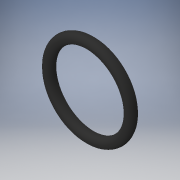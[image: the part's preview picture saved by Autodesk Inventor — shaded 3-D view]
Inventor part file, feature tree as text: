
AUTODESK INVENTOR PART (.ipt)
format: ipt  version: 2018 (Build 220112000, 112)  size: 136,704 bytes
history: native  units: in
note: dims shown in document units (in); Inventor stores cm internally (conversion verified against a paired STEP export)
features: revolve x1
ambient origin geometry x8: Origin, YZ Plane, XZ Plane, XY Plane, X Axis, Y Axis, Z Axis, Center Point
bodies: Solid1 (feature_tree)
feature tree (1):
  revolve  "Revolve1"  [1 undecoded]
note: 1 required parameter value undecoded (feature->parameter linkage not recoverable at this tier; creation-order binding heuristic only, values carry confidence <= 0.55)
